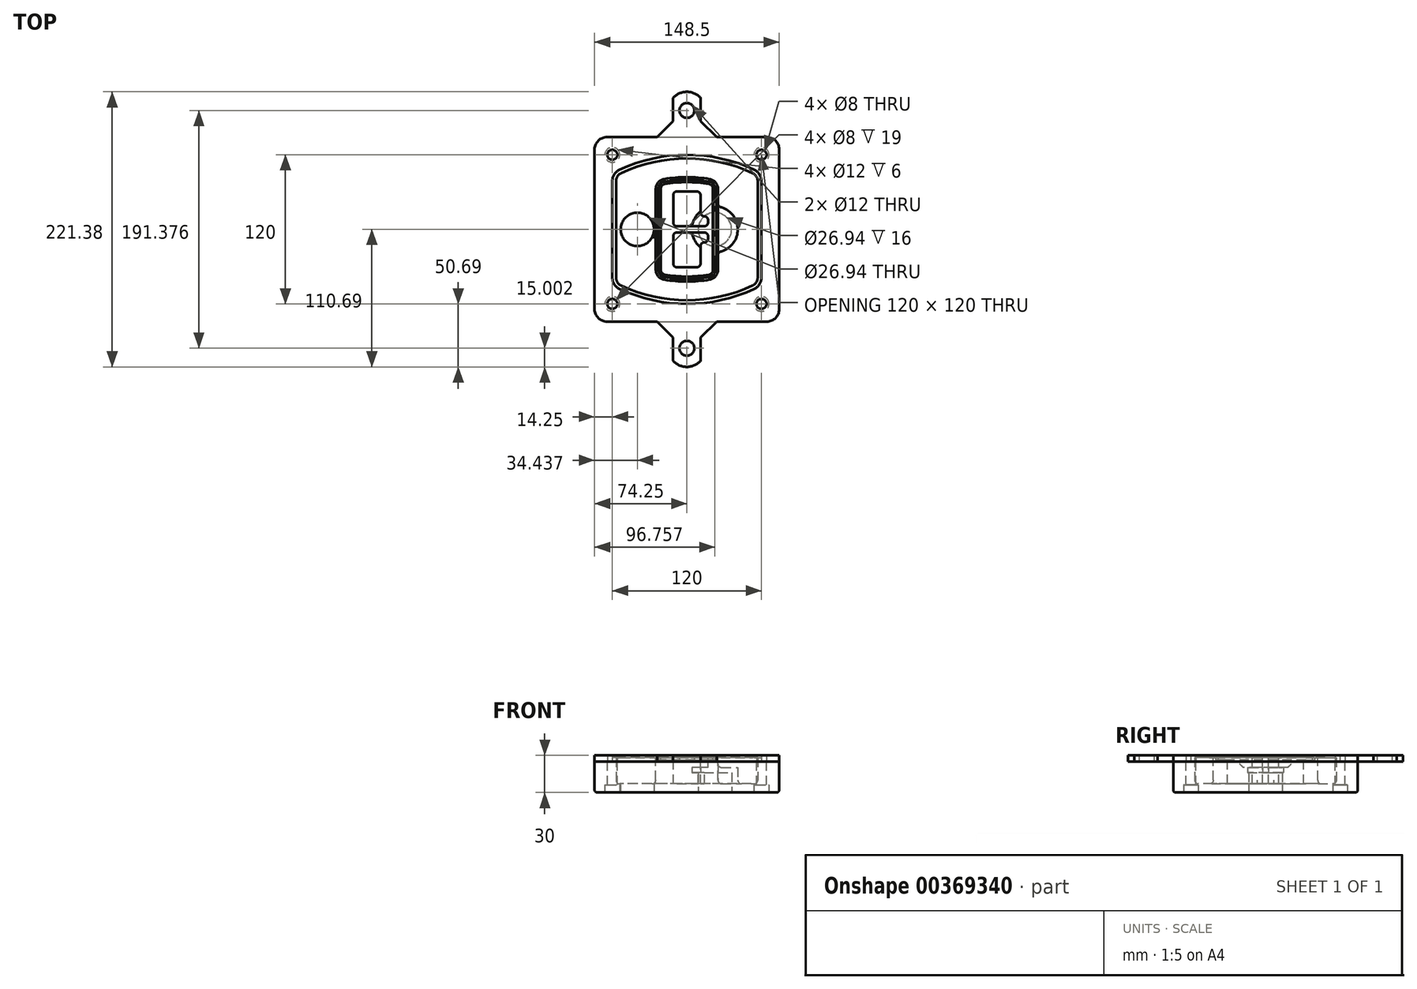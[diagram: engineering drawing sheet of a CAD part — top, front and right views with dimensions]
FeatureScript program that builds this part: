
annotation { "Feature Type Name" : "Feature", "Feature Type Description" : "" }
export const myFeature = defineFeature(function(context is Context, id is Id, definition is map)
    precondition{}
    {
        {
            var Q0;
            Q0=qCreatedBy(makeId("Top.planeOp"),FACE);
            var sketch = newSketch(context, id + "F0", { "sketchPlane" : qUnion([Q0])});
            skPoint(sketch, "E0.rect.middle", {"position": v(0, 0) * mm});
            skLineSegment(sketch, "E1.bottom", {"start": v(-64.25, -74.25) * mm, "end": v(64.25, -74.25) * mm});
            skLineSegment(sketch, "E1.top", {"start": v(-64.25, 74.25) * mm, "end": v(64.25, 74.25) * mm});
            skLineSegment(sketch, "E1.left", {"start": v(-74.25, -64.25) * mm, "end": v(-74.25, 64.25) * mm});
            skLineSegment(sketch, "E1.right", {"start": v(74.25, -64.25) * mm, "end": v(74.25, 64.25) * mm});
            skLineSegment(sketch, "E2", {"start": v(-74.25, 74.25) * mm, "end": v(74.25, -74.25) * mm, "construction": true});
            skLineSegment(sketch, "E3", {"start": v(74.25, 74.25) * mm, "end": v(-74.25, -74.25) * mm, "construction": true});
            skCircle(sketch, "E4", {"center": v(-60, 60) * mm, "radius": 4 * mm});
            skCircle(sketch, "E5", {"center": v(60, 60) * mm, "radius": 4 * mm});
            skCircle(sketch, "E6", {"center": v(60, -60) * mm, "radius": 4 * mm});
            skCircle(sketch, "E7", {"center": v(-60, -60) * mm, "radius": 4 * mm});
            skLineSegment(sketch, "E8", {"start": v(-60, 60) * mm, "end": v(60, 60) * mm, "construction": true});
            skLineSegment(sketch, "E9", {"start": v(60, 60) * mm, "end": v(60, -60) * mm, "construction": true});
            skLineSegment(sketch, "E10", {"start": v(60, -60) * mm, "end": v(-60, -60) * mm, "construction": true});
            skLineSegment(sketch, "E11", {"start": v(-60, -60) * mm, "end": v(-60, 60) * mm, "construction": true});
            skLineSegment(sketch, "E12", {"start": v(-60, 38.83) * mm, "end": v(-60, -38.83) * mm});
            skLineSegment(sketch, "E13", {"start": v(60, 38.83) * mm, "end": v(60, -38.83) * mm});
            skArc(sketch, "E14", {"start": v(54.26, 47.88) * mm, "mid": v(0, 60) * mm, "end": v(-54.26, 47.88) * mm});
            skArc(sketch, "E15", {"start": v(-54.26, -47.88) * mm, "mid": v(0, -60) * mm, "end": v(54.26, -47.88) * mm});
            skLineSegment(sketch, "E16", {"start": v(-60, 0) * mm, "end": v(60, 0) * mm, "construction": true});
            skPoint(sketch, "E17.visualSharp", {"position": v(-60, -45) * mm});
            skArc(sketch, "E17.filletArc", {"start": v(-60, -38.83) * mm, "mid": v(-58.44, -44.2) * mm, "end": v(-54.26, -47.88) * mm});
            skPoint(sketch, "E18.visualSharp", {"position": v(-60, 45) * mm});
            skArc(sketch, "E18.filletArc", {"start": v(-54.26, 47.88) * mm, "mid": v(-58.44, 44.2) * mm, "end": v(-60, 38.83) * mm});
            skPoint(sketch, "E19.visualSharp", {"position": v(60, 45) * mm});
            skArc(sketch, "E19.filletArc", {"start": v(60, 38.83) * mm, "mid": v(58.44, 44.2) * mm, "end": v(54.26, 47.88) * mm});
            skPoint(sketch, "E20.visualSharp", {"position": v(60, -45) * mm});
            skArc(sketch, "E20.filletArc", {"start": v(54.26, -47.88) * mm, "mid": v(58.44, -44.2) * mm, "end": v(60, -38.83) * mm});
            skPoint(sketch, "E21.visualSharp", {"position": v(-74.25, 74.25) * mm});
            skArc(sketch, "E21.filletArc", {"start": v(-64.25, 74.25) * mm, "mid": v(-71.32, 71.32) * mm, "end": v(-74.25, 64.25) * mm});
            skPoint(sketch, "E22.visualSharp", {"position": v(74.25, 74.25) * mm});
            skArc(sketch, "E22.filletArc", {"start": v(74.25, 64.25) * mm, "mid": v(71.32, 71.32) * mm, "end": v(64.25, 74.25) * mm});
            skPoint(sketch, "E23.visualSharp", {"position": v(74.25, -74.25) * mm});
            skArc(sketch, "E23.filletArc", {"start": v(64.25, -74.25) * mm, "mid": v(71.32, -71.32) * mm, "end": v(74.25, -64.25) * mm});
            skPoint(sketch, "E24.visualSharp", {"position": v(-74.25, -74.25) * mm});
            skArc(sketch, "E24.filletArc", {"start": v(-74.25, -64.25) * mm, "mid": v(-71.32, -71.32) * mm, "end": v(-64.25, -74.25) * mm});
            skArc(sketch, "E25.0", {"start": v(57, 38.83) * mm, "mid": v(55.9, 42.58) * mm, "end": v(52.98, 45.17) * mm});
            skLineSegment(sketch, "E25.1", {"start": v(57, 38.83) * mm, "end": v(57, -38.83) * mm});
            skArc(sketch, "E25.2", {"start": v(52.98, -45.17) * mm, "mid": v(55.9, -42.58) * mm, "end": v(57, -38.83) * mm});
            skArc(sketch, "E25.3", {"start": v(-52.98, -45.17) * mm, "mid": v(0, -57) * mm, "end": v(52.98, -45.17) * mm});
            skArc(sketch, "E25.4", {"start": v(-57, -38.83) * mm, "mid": v(-55.9, -42.58) * mm, "end": v(-52.98, -45.17) * mm});
            skArc(sketch, "E25.5", {"start": v(52.98, 45.17) * mm, "mid": v(0, 57) * mm, "end": v(-52.98, 45.17) * mm});
            skLineSegment(sketch, "E25.6", {"start": v(-57, 38.83) * mm, "end": v(-57, -38.83) * mm});
            skArc(sketch, "E25.7", {"start": v(-52.98, 45.17) * mm, "mid": v(-55.9, 42.58) * mm, "end": v(-57, 38.83) * mm});
            skArc(sketch, "E26.0", {"start": v(-55.96, 51.5) * mm, "mid": v(-61.82, 46.33) * mm, "end": v(-64, 38.83) * mm});
            skArc(sketch, "E26.1", {"start": v(55.96, 51.5) * mm, "mid": v(0, 64) * mm, "end": v(-55.96, 51.5) * mm});
            skArc(sketch, "E26.2", {"start": v(64, 38.83) * mm, "mid": v(61.82, 46.33) * mm, "end": v(55.96, 51.5) * mm});
            skLineSegment(sketch, "E26.3", {"start": v(64, 38.83) * mm, "end": v(64, -38.83) * mm});
            skArc(sketch, "E26.4", {"start": v(55.96, -51.5) * mm, "mid": v(61.82, -46.33) * mm, "end": v(64, -38.83) * mm});
            skLineSegment(sketch, "E26.5", {"start": v(-64, 38.83) * mm, "end": v(-64, -38.83) * mm});
            skArc(sketch, "E26.6", {"start": v(-55.96, -51.5) * mm, "mid": v(0, -64) * mm, "end": v(55.96, -51.5) * mm});
            skArc(sketch, "E26.7", {"start": v(-64, -38.83) * mm, "mid": v(-61.82, -46.33) * mm, "end": v(-55.96, -51.5) * mm});
            skSolve(sketch);
        }
        {
            var Q0;
            Q0=makeQuery(id+"F0.imprint","IMPRINT",FACE,{"disambiguationData":[TD([[makeQuery(id+"F0.imprint","IMPRINT",EDGE,{"derivedFrom":sQuery(id+"F0.wireOp",EDGE,"E1.bottom")}),1.0]])]});
            var Q1;
            Q1=makeQuery(id+"F0.imprint","IMPRINT",FACE,{"disambiguationData":[TD([[makeQuery(id+"F0.imprint","IMPRINT",EDGE,{"derivedFrom":sQuery(id+"F0.wireOp",EDGE,"E12")}),1.0]])]});
            var Q2;
            Q2=makeQuery(id+"F0.imprint","IMPRINT",FACE,{"disambiguationData":[TD([[makeQuery(id+"F0.imprint","IMPRINT",EDGE,{"derivedFrom":sQuery(id+"F0.wireOp",EDGE,"E25.0")}),1.0]])]});
            var Q3;
            Q3=makeQuery(id+"F0.imprint","IMPRINT",FACE,{"disambiguationData":[TD([[makeQuery(id+"F0.imprint","IMPRINT",EDGE,{"derivedFrom":sQuery(id+"F0.wireOp",EDGE,"E12")}),-1.0]])]});
            extrude(context, id + "F1", {"entities" : qUnion([Q0, Q1, Q2, Q3]), "oppositeDirection" : true, "depth" : 25 * mm});
        }
        {
            var Q0;
            Q0=makeQuery(id+"F0.imprint","IMPRINT",FACE,{"disambiguationData":[TD([[makeQuery(id+"F0.imprint","IMPRINT",EDGE,{"derivedFrom":sQuery(id+"F0.wireOp",EDGE,"E12")}),1.0]])]});
            extrude(context, id + "F2", {"entities" : qUnion([Q0]), "operationType" : NewBodyOperationType.ADD, "depth" : 3 * mm});
        }
        {
            var Q0;
            Q0=makeQuery(id+"F0.imprint","IMPRINT",FACE,{"disambiguationData":[TD([[makeQuery(id+"F0.imprint","IMPRINT",EDGE,{"derivedFrom":sQuery(id+"F0.wireOp",EDGE,"E25.0")}),1.0]])]});
            extrude(context, id + "F3", {"entities" : qUnion([Q0]), "operationType" : NewBodyOperationType.REMOVE, "oppositeDirection" : true, "depth" : 18 * mm});
        }
        {
            var Q0;
            Q0=makeQuery(id+"F2.opExtrude","CAP_FACE",FACE,{"disambiguationData":[OSD([sQuery(id+"F0.wireOp",EDGE,"E12"),sQuery(id+"F0.wireOp",EDGE,"E13"),sQuery(id+"F0.wireOp",EDGE,"E14"),sQuery(id+"F0.wireOp",EDGE,"E15"),sQuery(id+"F0.wireOp",EDGE,"E17.filletArc"),sQuery(id+"F0.wireOp",EDGE,"E18.filletArc"),sQuery(id+"F0.wireOp",EDGE,"E19.filletArc"),sQuery(id+"F0.wireOp",EDGE,"E20.filletArc"),sQuery(id+"F0.wireOp",EDGE,"E25.0"),sQuery(id+"F0.wireOp",EDGE,"E25.1"),sQuery(id+"F0.wireOp",EDGE,"E25.2"),sQuery(id+"F0.wireOp",EDGE,"E25.3"),sQuery(id+"F0.wireOp",EDGE,"E25.4"),sQuery(id+"F0.wireOp",EDGE,"E25.5"),sQuery(id+"F0.wireOp",EDGE,"E25.6"),sQuery(id+"F0.wireOp",EDGE,"E25.7")])],"isStart":false});
            var sketch = newSketch(context, id + "F4", { "sketchPlane" : qUnion([Q0])});
            skArc(sketch, "E27.0", {"start": v(-18.34, -40.45) * mm, "mid": v(0, -42) * mm, "end": v(18.34, -40.45) * mm});
            skArc(sketch, "E28.0", {"start": v(18.34, 40.45) * mm, "mid": v(0, 42) * mm, "end": v(-18.34, 40.45) * mm});
            skLineSegment(sketch, "E29", {"start": v(-25, 32.57) * mm, "end": v(-25, -32.57) * mm});
            skLineSegment(sketch, "E30", {"start": v(25, 32.57) * mm, "end": v(25, -32.57) * mm});
            skLineSegment(sketch, "E31", {"start": v(-25, 39.1) * mm, "end": v(25, 39.1) * mm, "construction": true});
            skLineSegment(sketch, "E32", {"start": v(-25, -39.1) * mm, "end": v(25, -39.1) * mm, "construction": true});
            skPoint(sketch, "E33.visualSharp", {"position": v(-25, 39.1) * mm});
            skArc(sketch, "E33.filletArc", {"start": v(-18.34, 40.45) * mm, "mid": v(-23.11, 37.73) * mm, "end": v(-25, 32.57) * mm});
            skPoint(sketch, "E34.visualSharp", {"position": v(25, 39.1) * mm});
            skArc(sketch, "E34.filletArc", {"start": v(25, 32.57) * mm, "mid": v(23.11, 37.73) * mm, "end": v(18.34, 40.45) * mm});
            skPoint(sketch, "E35.visualSharp", {"position": v(25, -39.1) * mm});
            skArc(sketch, "E35.filletArc", {"start": v(18.34, -40.45) * mm, "mid": v(23.11, -37.73) * mm, "end": v(25, -32.57) * mm});
            skPoint(sketch, "E36.visualSharp", {"position": v(-25, -39.1) * mm});
            skArc(sketch, "E36.filletArc", {"start": v(-25, -32.57) * mm, "mid": v(-23.11, -37.73) * mm, "end": v(-18.34, -40.45) * mm});
            skArc(sketch, "E37.0", {"start": v(52.98, 45.17) * mm, "mid": v(0, 57) * mm, "end": v(-52.98, 45.17) * mm});
            skArc(sketch, "E37.1", {"start": v(-52.98, 45.17) * mm, "mid": v(-55.9, 42.58) * mm, "end": v(-57, 38.83) * mm});
            skLineSegment(sketch, "E37.2", {"start": v(-57, 38.83) * mm, "end": v(-57, -38.83) * mm});
            skArc(sketch, "E37.3", {"start": v(-57, -38.83) * mm, "mid": v(-55.9, -42.58) * mm, "end": v(-52.98, -45.17) * mm});
            skArc(sketch, "E37.4", {"start": v(-52.98, -45.17) * mm, "mid": v(0, -57) * mm, "end": v(52.98, -45.17) * mm});
            skArc(sketch, "E37.5", {"start": v(52.98, -45.17) * mm, "mid": v(55.9, -42.58) * mm, "end": v(57, -38.83) * mm});
            skLineSegment(sketch, "E37.6", {"start": v(57, 38.83) * mm, "end": v(57, -38.83) * mm});
            skArc(sketch, "E37.7", {"start": v(57, 38.83) * mm, "mid": v(55.9, 42.58) * mm, "end": v(52.98, 45.17) * mm});
            skLineSegment(sketch, "E38.0", {"start": v(23, 32.57) * mm, "end": v(23, -32.57) * mm});
            skArc(sketch, "E38.1", {"start": v(18, -38.48) * mm, "mid": v(21.58, -36.44) * mm, "end": v(23, -32.57) * mm});
            skArc(sketch, "E38.2", {"start": v(-18, -38.48) * mm, "mid": v(0, -40) * mm, "end": v(18, -38.48) * mm});
            skArc(sketch, "E38.3", {"start": v(-23, -32.57) * mm, "mid": v(-21.58, -36.44) * mm, "end": v(-18, -38.48) * mm});
            skLineSegment(sketch, "E38.4", {"start": v(-23, 32.57) * mm, "end": v(-23, -32.57) * mm});
            skArc(sketch, "E38.5", {"start": v(23, 32.57) * mm, "mid": v(21.58, 36.44) * mm, "end": v(18, 38.48) * mm});
            skArc(sketch, "E38.6", {"start": v(-18, 38.48) * mm, "mid": v(-21.58, 36.44) * mm, "end": v(-23, 32.57) * mm});
            skArc(sketch, "E38.7", {"start": v(18, 38.48) * mm, "mid": v(0, 40) * mm, "end": v(-18, 38.48) * mm});
            skArc(sketch, "E39.0", {"start": v(21, 32.57) * mm, "mid": v(20.06, 35.15) * mm, "end": v(17.67, 36.5) * mm});
            skLineSegment(sketch, "E39.1", {"start": v(21, 32.57) * mm, "end": v(21, -32.57) * mm});
            skArc(sketch, "E39.2", {"start": v(17.67, -36.5) * mm, "mid": v(20.06, -35.15) * mm, "end": v(21, -32.57) * mm});
            skArc(sketch, "E39.3", {"start": v(-17.67, -36.5) * mm, "mid": v(0, -38) * mm, "end": v(17.67, -36.5) * mm});
            skArc(sketch, "E39.4", {"start": v(-21, -32.57) * mm, "mid": v(-20.06, -35.15) * mm, "end": v(-17.67, -36.5) * mm});
            skArc(sketch, "E39.5", {"start": v(17.67, 36.5) * mm, "mid": v(0, 38) * mm, "end": v(-17.67, 36.5) * mm});
            skLineSegment(sketch, "E39.6", {"start": v(-21, 32.57) * mm, "end": v(-21, -32.57) * mm});
            skArc(sketch, "E39.7", {"start": v(-17.67, 36.5) * mm, "mid": v(-20.06, 35.15) * mm, "end": v(-21, 32.57) * mm});
            skLineSegment(sketch, "E40", {"start": v(-25, 0) * mm, "end": v(25, 0) * mm, "construction": true});
            skLineSegment(sketch, "E41", {"start": v(-11, 5.5) * mm, "end": v(-11, 27.5) * mm});
            skLineSegment(sketch, "E42", {"start": v(-8, 30.5) * mm, "end": v(8, 30.5) * mm});
            skLineSegment(sketch, "E43", {"start": v(11, 27.5) * mm, "end": v(11, 13.5) * mm});
            skLineSegment(sketch, "E44", {"start": v(14, 10.5) * mm, "end": v(14, 10.5) * mm});
            skLineSegment(sketch, "E45", {"start": v(17, 7.5) * mm, "end": v(17, 5.5) * mm});
            skLineSegment(sketch, "E46", {"start": v(14, 2.5) * mm, "end": v(-8, 2.5) * mm});
            skPoint(sketch, "E47.visualSharp", {"position": v(-11, 30.5) * mm});
            skArc(sketch, "E47.filletArc", {"start": v(-8, 30.5) * mm, "mid": v(-10.12, 29.62) * mm, "end": v(-11, 27.5) * mm});
            skPoint(sketch, "E48.visualSharp", {"position": v(11, 30.5) * mm});
            skArc(sketch, "E48.filletArc", {"start": v(11, 27.5) * mm, "mid": v(10.12, 29.62) * mm, "end": v(8, 30.5) * mm});
            skPoint(sketch, "E49.visualSharp", {"position": v(11, 10.5) * mm});
            skArc(sketch, "E49.filletArc", {"start": v(11, 13.5) * mm, "mid": v(11.88, 11.38) * mm, "end": v(14, 10.5) * mm});
            skPoint(sketch, "E50.visualSharp", {"position": v(17, 10.5) * mm});
            skArc(sketch, "E50.filletArc", {"start": v(17, 7.5) * mm, "mid": v(16.12, 9.62) * mm, "end": v(14, 10.5) * mm});
            skPoint(sketch, "E51.visualSharp", {"position": v(17, 2.5) * mm});
            skArc(sketch, "E51.filletArc", {"start": v(14, 2.5) * mm, "mid": v(16.12, 3.38) * mm, "end": v(17, 5.5) * mm});
            skPoint(sketch, "E52.visualSharp", {"position": v(-11, 2.5) * mm});
            skArc(sketch, "E52.filletArc", {"start": v(-11, 5.5) * mm, "mid": v(-10.12, 3.38) * mm, "end": v(-8, 2.5) * mm});
            skLineSegment(sketch, "E53.0.MirrorCS", {"start": v(14, -2.5) * mm, "end": v(-8, -2.5) * mm});
            skArc(sketch, "E54.0.MirrorCS", {"start": v(-11, -5.5) * mm, "mid": v(-10.12, -3.38) * mm, "end": v(-8, -2.5) * mm});
            skLineSegment(sketch, "E55.0.MirrorCS", {"start": v(-11, -5.5) * mm, "end": v(-11, -27.5) * mm});
            skArc(sketch, "E56.0.MirrorCS", {"start": v(-8, -30.5) * mm, "mid": v(-10.12, -29.62) * mm, "end": v(-11, -27.5) * mm});
            skLineSegment(sketch, "E57.0.MirrorCS", {"start": v(-8, -30.5) * mm, "end": v(8, -30.5) * mm});
            skArc(sketch, "E58.0.MirrorCS", {"start": v(11, -27.5) * mm, "mid": v(10.12, -29.62) * mm, "end": v(8, -30.5) * mm});
            skLineSegment(sketch, "E59.0.MirrorCS", {"start": v(11, -27.5) * mm, "end": v(11, -13.5) * mm});
            skArc(sketch, "E60.0.MirrorCS", {"start": v(11, -13.5) * mm, "mid": v(11.88, -11.38) * mm, "end": v(14, -10.5) * mm});
            skArc(sketch, "E61.0.MirrorCS", {"start": v(17, -7.5) * mm, "mid": v(16.12, -9.62) * mm, "end": v(14, -10.5) * mm});
            skLineSegment(sketch, "E62.0.MirrorCS", {"start": v(17, -7.5) * mm, "end": v(17, -5.5) * mm});
            skArc(sketch, "E63.0.MirrorCS", {"start": v(14, -2.5) * mm, "mid": v(16.12, -3.38) * mm, "end": v(17, -5.5) * mm});
            skSolve(sketch);
        }
        {
            var Q0;
            Q0=makeQuery(id+"F4.imprint","IMPRINT",FACE,{"disambiguationData":[TD([[makeQuery(id+"F4.imprint","IMPRINT",EDGE,{"derivedFrom":sQuery(id+"F4.wireOp",EDGE,"E27.0")}),1.0]])]});
            var Q1;
            Q1=makeQuery(id+"F4.imprint","IMPRINT",FACE,{"disambiguationData":[TD([[makeQuery(id+"F4.imprint","IMPRINT",EDGE,{"derivedFrom":sQuery(id+"F4.wireOp",EDGE,"E38.0")}),-1.0]])]});
            var Q2;
            Q2=makeQuery(id+"F4.imprint","IMPRINT",FACE,{"disambiguationData":[TD([[makeQuery(id+"F4.imprint","IMPRINT",EDGE,{"derivedFrom":sQuery(id+"F4.wireOp",EDGE,"E39.0")}),1.0]])]});
            extrude(context, id + "F5", {"entities" : qUnion([Q0, Q1, Q2]), "operationType" : NewBodyOperationType.ADD, "endBound" : BoundingType.UP_TO_NEXT, "oppositeDirection" : true, "depth" : 25 * mm});
        }
        {
            var Q0;
            Q0=makeQuery(id+"F4.imprint","IMPRINT",FACE,{"disambiguationData":[TD([[makeQuery(id+"F4.imprint","IMPRINT",EDGE,{"derivedFrom":sQuery(id+"F4.wireOp",EDGE,"E38.0")}),-1.0]])]});
            extrude(context, id + "F6", {"entities" : qUnion([Q0]), "operationType" : NewBodyOperationType.REMOVE, "oppositeDirection" : true, "depth" : 2 * mm});
        }
        {
            var Q0;
            Q0=makeQuery(id+"F1.opExtrude","CAP_FACE",FACE,{"disambiguationData":[OSD([sQuery(id+"F0.wireOp",EDGE,"E1.bottom"),sQuery(id+"F0.wireOp",EDGE,"E1.top"),sQuery(id+"F0.wireOp",EDGE,"E1.left"),sQuery(id+"F0.wireOp",EDGE,"E1.right"),sQuery(id+"F0.wireOp",EDGE,"E4"),sQuery(id+"F0.wireOp",EDGE,"E5"),sQuery(id+"F0.wireOp",EDGE,"E6"),sQuery(id+"F0.wireOp",EDGE,"E7"),sQuery(id+"F0.wireOp",EDGE,"E21.filletArc"),sQuery(id+"F0.wireOp",EDGE,"E22.filletArc"),sQuery(id+"F0.wireOp",EDGE,"E23.filletArc"),sQuery(id+"F0.wireOp",EDGE,"E24.filletArc")])],"isStart":false});
            var sketch = newSketch(context, id + "F7", { "sketchPlane" : qUnion([Q0])});
            skCircle(sketch, "E64", {"center": v(22.5, 0) * mm, "radius": 13.47 * mm});
            skCircle(sketch, "E65", {"center": v(-39.81, 0) * mm, "radius": 13.47 * mm});
            skLineSegment(sketch, "E66", {"start": v(74.25, 0) * mm, "end": v(-74.25, 0) * mm});
            skCircle(sketch, "E67", {"center": v(22.5, 0) * mm, "radius": 18.47 * mm});
            skCircle(sketch, "E68", {"center": v(60, -60) * mm, "radius": 6 * mm});
            skCircle(sketch, "E69", {"center": v(-60, -60) * mm, "radius": 6 * mm});
            skCircle(sketch, "E70", {"center": v(-60, 60) * mm, "radius": 6 * mm});
            skCircle(sketch, "E71", {"center": v(60, 60) * mm, "radius": 6 * mm});
            skSolve(sketch);
        }
        {
            var Q0;
            {var subQ1=sQuery(id+"F7.wireOp",EDGE,"E66");var subQ4=sQuery(id+"F7.wireOp",EDGE,"E64");var subQ6=makeQuery(id+"F7.imprint","INTERSECT",VERTEX,{"disambiguationData":[OD(0.0)],"derivedFrom":[subQ4,subQ1]});Q0=makeQuery(id+"F7.imprint","IMPRINT",FACE,{"disambiguationData":[TD([[makeQuery(id+"F7.imprint","IMPRINT",EDGE,{"disambiguationData":[TD([[subQ6,-1.0]])],"derivedFrom":subQ4}),-1.0]])]});}
            var Q1;
            {var subQ0=sQuery(id+"F7.wireOp",EDGE,"E66");var subQ1=sQuery(id+"F7.wireOp",EDGE,"E64");var subQ3=makeQuery(id+"F7.imprint","INTERSECT",VERTEX,{"disambiguationData":[OD(0.0)],"derivedFrom":[subQ1,subQ0]});Q1=makeQuery(id+"F7.imprint","IMPRINT",FACE,{"disambiguationData":[TD([[makeQuery(id+"F7.imprint","IMPRINT",EDGE,{"disambiguationData":[TD([[subQ3,-1.0]])],"derivedFrom":subQ1}),1.0]])]});}
            var Q2;
            {var subQ0=sQuery(id+"F7.wireOp",EDGE,"E66");var subQ1=sQuery(id+"F7.wireOp",EDGE,"E64");var subQ3=makeQuery(id+"F7.imprint","INTERSECT",VERTEX,{"disambiguationData":[OD(0.0)],"derivedFrom":[subQ1,subQ0]});Q2=makeQuery(id+"F7.imprint","IMPRINT",FACE,{"disambiguationData":[TD([[makeQuery(id+"F7.imprint","IMPRINT",EDGE,{"disambiguationData":[TD([[subQ3,1.0]])],"derivedFrom":subQ1}),1.0]])]});}
            var Q3;
            {var subQ1=sQuery(id+"F7.wireOp",EDGE,"E66");var subQ4=sQuery(id+"F7.wireOp",EDGE,"E64");var subQ6=makeQuery(id+"F7.imprint","INTERSECT",VERTEX,{"disambiguationData":[OD(0.0)],"derivedFrom":[subQ4,subQ1]});Q3=makeQuery(id+"F7.imprint","IMPRINT",FACE,{"disambiguationData":[TD([[makeQuery(id+"F7.imprint","IMPRINT",EDGE,{"disambiguationData":[TD([[subQ6,1.0]])],"derivedFrom":subQ4}),-1.0]])]});}
            extrude(context, id + "F8", {"entities" : qUnion([Q0, Q1, Q2, Q3]), "operationType" : NewBodyOperationType.ADD, "oppositeDirection" : true, "depth" : 20 * mm});
        }
        {
            var Q0;
            {var subQ0=sQuery(id+"F7.wireOp",EDGE,"E66");var subQ1=sQuery(id+"F7.wireOp",EDGE,"E64");var subQ3=makeQuery(id+"F7.imprint","INTERSECT",VERTEX,{"disambiguationData":[OD(0.0)],"derivedFrom":[subQ1,subQ0]});Q0=makeQuery(id+"F7.imprint","IMPRINT",FACE,{"disambiguationData":[TD([[makeQuery(id+"F7.imprint","IMPRINT",EDGE,{"disambiguationData":[TD([[subQ3,-1.0]])],"derivedFrom":subQ1}),1.0]])]});}
            var Q1;
            {var subQ0=sQuery(id+"F7.wireOp",EDGE,"E66");var subQ1=sQuery(id+"F7.wireOp",EDGE,"E64");var subQ3=makeQuery(id+"F7.imprint","INTERSECT",VERTEX,{"disambiguationData":[OD(0.0)],"derivedFrom":[subQ1,subQ0]});Q1=makeQuery(id+"F7.imprint","IMPRINT",FACE,{"disambiguationData":[TD([[makeQuery(id+"F7.imprint","IMPRINT",EDGE,{"disambiguationData":[TD([[subQ3,1.0]])],"derivedFrom":subQ1}),1.0]])]});}
            extrude(context, id + "F9", {"entities" : qUnion([Q0, Q1]), "operationType" : NewBodyOperationType.REMOVE, "oppositeDirection" : true, "depth" : 16 * mm});
        }
        {
            var Q0;
            {var subQ0=sQuery(id+"F7.wireOp",EDGE,"E66");var subQ1=sQuery(id+"F7.wireOp",EDGE,"E65");var subQ3=makeQuery(id+"F7.imprint","INTERSECT",VERTEX,{"disambiguationData":[OD(0.0)],"derivedFrom":[subQ1,subQ0]});Q0=makeQuery(id+"F7.imprint","IMPRINT",FACE,{"disambiguationData":[TD([[makeQuery(id+"F7.imprint","IMPRINT",EDGE,{"disambiguationData":[TD([[subQ3,-1.0]])],"derivedFrom":subQ1}),1.0]])]});}
            var Q1;
            {var subQ0=sQuery(id+"F7.wireOp",EDGE,"E66");var subQ1=sQuery(id+"F7.wireOp",EDGE,"E65");var subQ3=makeQuery(id+"F7.imprint","INTERSECT",VERTEX,{"disambiguationData":[OD(0.0)],"derivedFrom":[subQ1,subQ0]});Q1=makeQuery(id+"F7.imprint","IMPRINT",FACE,{"disambiguationData":[TD([[makeQuery(id+"F7.imprint","IMPRINT",EDGE,{"disambiguationData":[TD([[subQ3,1.0]])],"derivedFrom":subQ1}),1.0]])]});}
            extrude(context, id + "F10", {"entities" : qUnion([Q0, Q1]), "operationType" : NewBodyOperationType.REMOVE, "oppositeDirection" : true, "depth" : 25 * mm});
        }
        {
            var Q0;
            Q0=makeQuery(id+"F7.imprint","IMPRINT",FACE,{"disambiguationData":[TD([[makeQuery(id+"F7.imprint","IMPRINT",EDGE,{"derivedFrom":sQuery(id+"F7.wireOp",EDGE,"E68")}),1.0]])]});
            var Q1;
            Q1=makeQuery(id+"F7.imprint","IMPRINT",FACE,{"disambiguationData":[TD([[makeQuery(id+"F7.imprint","IMPRINT",EDGE,{"derivedFrom":makeQuery(id+"F1.opExtrude","CAP_EDGE",EDGE,{"disambiguationData":[OSD([sQuery(id+"F0.wireOp",EDGE,"E5")])],"isStart":false})}),-1.0]])]});
            var Q2;
            Q2=makeQuery(id+"F7.imprint","IMPRINT",FACE,{"disambiguationData":[TD([[makeQuery(id+"F7.imprint","IMPRINT",EDGE,{"derivedFrom":sQuery(id+"F7.wireOp",EDGE,"E69")}),1.0]])]});
            var Q3;
            Q3=makeQuery(id+"F7.imprint","IMPRINT",FACE,{"disambiguationData":[TD([[makeQuery(id+"F7.imprint","IMPRINT",EDGE,{"derivedFrom":makeQuery(id+"F1.opExtrude","CAP_EDGE",EDGE,{"disambiguationData":[OSD([sQuery(id+"F0.wireOp",EDGE,"E4")])],"isStart":false})}),-1.0]])]});
            var Q4;
            Q4=makeQuery(id+"F7.imprint","IMPRINT",FACE,{"disambiguationData":[TD([[makeQuery(id+"F7.imprint","IMPRINT",EDGE,{"derivedFrom":sQuery(id+"F7.wireOp",EDGE,"E70")}),1.0]])]});
            var Q5;
            Q5=makeQuery(id+"F7.imprint","IMPRINT",FACE,{"disambiguationData":[TD([[makeQuery(id+"F7.imprint","IMPRINT",EDGE,{"derivedFrom":makeQuery(id+"F1.opExtrude","CAP_EDGE",EDGE,{"disambiguationData":[OSD([sQuery(id+"F0.wireOp",EDGE,"E7")])],"isStart":false})}),-1.0]])]});
            var Q6;
            Q6=makeQuery(id+"F7.imprint","IMPRINT",FACE,{"disambiguationData":[TD([[makeQuery(id+"F7.imprint","IMPRINT",EDGE,{"derivedFrom":sQuery(id+"F7.wireOp",EDGE,"E71")}),1.0]])]});
            var Q7;
            Q7=makeQuery(id+"F7.imprint","IMPRINT",FACE,{"disambiguationData":[TD([[makeQuery(id+"F7.imprint","IMPRINT",EDGE,{"derivedFrom":makeQuery(id+"F1.opExtrude","CAP_EDGE",EDGE,{"disambiguationData":[OSD([sQuery(id+"F0.wireOp",EDGE,"E6")])],"isStart":false})}),-1.0]])]});
            extrude(context, id + "F11", {"entities" : qUnion([Q0, Q1, Q2, Q3, Q4, Q5, Q6, Q7]), "operationType" : NewBodyOperationType.REMOVE, "oppositeDirection" : true, "depth" : 6 * mm});
        }
        {
            var Q0;
            Q0=makeQuery(id+"F9.boolean.opBoolean","COPY",FACE,{"derivedFrom":makeQuery(id+"F9.opExtrude","CAP_FACE",FACE,{"disambiguationData":[OSD([sQuery(id+"F7.wireOp",EDGE,"E64")])],"isStart":false})});
            var sketch = newSketch(context, id + "F12", { "sketchPlane" : qUnion([Q0])});
            skArc(sketch, "E72.0", {"start": v(11, 14.45) * mm, "mid": v(6.45, 9.13) * mm, "end": v(4.2, 2.5) * mm});
            skArc(sketch, "E72.1", {"start": v(4.2, -2.5) * mm, "mid": v(6.45, -9.13) * mm, "end": v(11, -14.45) * mm});
            skLineSegment(sketch, "E73", {"start": v(4.2, -2.5) * mm, "end": v(14, -2.5) * mm});
            skLineSegment(sketch, "E74.0", {"start": v(14, 2.5) * mm, "end": v(4.2, 2.5) * mm});
            skArc(sketch, "E74.1", {"start": v(14, 2.5) * mm, "mid": v(16.12, 3.38) * mm, "end": v(17, 5.5) * mm});
            skLineSegment(sketch, "E74.2", {"start": v(17, 7.5) * mm, "end": v(17, 5.5) * mm});
            skArc(sketch, "E74.3", {"start": v(17, 7.5) * mm, "mid": v(16.12, 9.62) * mm, "end": v(14, 10.5) * mm});
            skArc(sketch, "E74.4", {"start": v(11, 13.5) * mm, "mid": v(11.88, 11.38) * mm, "end": v(14, 10.5) * mm});
            skLineSegment(sketch, "E74.5", {"start": v(11, 14.45) * mm, "end": v(11, 13.5) * mm});
            skLineSegment(sketch, "E74.7", {"start": v(14, -2.5) * mm, "end": v(4.2, -2.5) * mm});
            skArc(sketch, "E74.8", {"start": v(14, -2.5) * mm, "mid": v(16.12, -3.38) * mm, "end": v(17, -5.5) * mm});
            skLineSegment(sketch, "E74.9", {"start": v(17, -7.5) * mm, "end": v(17, -5.5) * mm});
            skArc(sketch, "E74.10", {"start": v(17, -7.5) * mm, "mid": v(16.12, -9.62) * mm, "end": v(14, -10.5) * mm});
            skArc(sketch, "E74.11", {"start": v(11, -13.5) * mm, "mid": v(11.88, -11.38) * mm, "end": v(14, -10.5) * mm});
            skLineSegment(sketch, "E74.12", {"start": v(11, -14.45) * mm, "end": v(11, -13.5) * mm});
            skPoint(sketch, "E75.orphan", {"position": v(11, -27.5) * mm});
            skPoint(sketch, "E76.orphan", {"position": v(-8, -2.5) * mm});
            skPoint(sketch, "E77.orphan", {"position": v(-8, 2.5) * mm});
            skPoint(sketch, "E78.orphan", {"position": v(11, 27.5) * mm});
            skSolve(sketch);
        }
        {
            var Q0;
            {var subQ7=sQuery(id+"F12.wireOp",EDGE,"E72.0");var subQ14=sQuery(id+"F12.wireOp",EDGE,"E72.1");var subQ16=sQuery(id+"F12.wireOp",EDGE,"E74.1");var subQ18=sQuery(id+"F12.wireOp",EDGE,"E74.8");Q0=qUnion([makeQuery(id+"F12.imprint","IMPRINT",FACE,{"disambiguationData":[TD([[makeQuery(id+"F12.imprint","IMPRINT",EDGE,{"derivedFrom":subQ7}),1.0]])]}),makeQuery(id+"F12.imprint","IMPRINT",FACE,{"disambiguationData":[TD([[makeQuery(id+"F12.imprint","IMPRINT",EDGE,{"derivedFrom":subQ14}),1.0]])]}),makeQuery(id+"F12.imprint","IMPRINT",FACE,{"disambiguationData":[TD([[makeQuery(id+"F12.imprint","IMPRINT",EDGE,{"derivedFrom":subQ16}),1.0]])]}),makeQuery(id+"F12.imprint","IMPRINT",FACE,{"disambiguationData":[TD([[makeQuery(id+"F12.imprint","IMPRINT",EDGE,{"derivedFrom":subQ18}),-1.0]])]})]);}
            var Q1;
            Q1=makeQuery(id+"F5.boolean.opBoolean","SPLIT",FACE,{"disambiguationData":[TD([makeQuery(id+"F5.opExtrude","SWEPT_FACE",FACE,{"disambiguationData":[OSD([sQuery(id+"F4.wireOp",EDGE,"E41")])]})])],"derivedFrom":makeQuery(id+"F3.boolean.opBoolean","COPY",FACE,{"derivedFrom":makeQuery(id+"F3.opExtrude","CAP_FACE",FACE,{"disambiguationData":[OSD([sQuery(id+"F0.wireOp",EDGE,"E25.0"),sQuery(id+"F0.wireOp",EDGE,"E25.1"),sQuery(id+"F0.wireOp",EDGE,"E25.2"),sQuery(id+"F0.wireOp",EDGE,"E25.3"),sQuery(id+"F0.wireOp",EDGE,"E25.4"),sQuery(id+"F0.wireOp",EDGE,"E25.5"),sQuery(id+"F0.wireOp",EDGE,"E25.6"),sQuery(id+"F0.wireOp",EDGE,"E25.7")])],"isStart":false})})});
            extrude(context, id + "F13", {"entities" : qUnion([Q0]), "operationType" : NewBodyOperationType.REMOVE, "endBound" : BoundingType.UP_TO_SURFACE, "endBoundEntityFace" : qUnion([Q1]), "depth" : 25 * mm});
        }
        {
            var Q0;
            Q0=makeQuery(id+"F3.boolean.opBoolean","COPY",EDGE,{"derivedFrom":makeQuery(id+"F3.opExtrude","CAP_EDGE",EDGE,{"disambiguationData":[OSD([sQuery(id+"F0.wireOp",EDGE,"E25.6")])],"isStart":false})});
            var Q1;
            Q1=makeQuery(id+"F8.boolean.opBoolean","INTERSECT",EDGE,{"derivedFrom":[makeQuery(id+"F5.opExtrude","SWEPT_FACE",FACE,{"disambiguationData":[OSD([sQuery(id+"F4.wireOp",EDGE,"E30")])]}),makeQuery(id+"F8.opExtrude","CAP_FACE",FACE,{"disambiguationData":[OSD([sQuery(id+"F7.wireOp",EDGE,"E67")])],"isStart":false})]});
            var Q2;
            Q2=makeQuery(id+"F8.boolean.opBoolean","INTERSECT",EDGE,{"disambiguationData":[OD(1.0)],"derivedFrom":[makeQuery(id+"F5.opExtrude","SWEPT_FACE",FACE,{"disambiguationData":[OSD([sQuery(id+"F4.wireOp",EDGE,"E30")])]}),makeQuery(id+"F8.opExtrude","SWEPT_FACE",FACE,{"disambiguationData":[OSD([sQuery(id+"F7.wireOp",EDGE,"E67")])]})]});
            var Q3;
            {var subQ0=sQuery(id+"F4.wireOp",EDGE,"E30");Q3=makeQuery(id+"F8.boolean.opBoolean","SPLIT",EDGE,{"disambiguationData":[TD([makeQuery(id+"F5.opExtrude","SWEPT_FACE",FACE,{"disambiguationData":[OSD([sQuery(id+"F4.wireOp",EDGE,"E35.filletArc")])]})])],"derivedFrom":makeQuery(id+"F5.opExtrude","CAP_EDGE",EDGE,{"disambiguationData":[OSD([subQ0])],"isStart":false})});}
            var Q4;
            {var subQ0=sQuery(id+"F0.wireOp",EDGE,"E25.7");var subQ1=sQuery(id+"F0.wireOp",EDGE,"E25.1");var subQ2=sQuery(id+"F0.wireOp",EDGE,"E25.6");var subQ3=sQuery(id+"F0.wireOp",EDGE,"E25.5");var subQ4=sQuery(id+"F0.wireOp",EDGE,"E25.4");var subQ5=sQuery(id+"F0.wireOp",EDGE,"E25.0");var subQ6=sQuery(id+"F0.wireOp",EDGE,"E25.2");var subQ7=sQuery(id+"F0.wireOp",EDGE,"E25.3");Q4=makeQuery(id+"F8.boolean.opBoolean","INTERSECT",EDGE,{"derivedFrom":[makeQuery(id+"F5.boolean.opBoolean","SPLIT",FACE,{"disambiguationData":[TD([makeQuery(id+"F2.opExtrude","SWEPT_FACE",FACE,{"disambiguationData":[OSD([subQ5])]})])],"derivedFrom":makeQuery(id+"F3.boolean.opBoolean","COPY",FACE,{"derivedFrom":makeQuery(id+"F3.opExtrude","CAP_FACE",FACE,{"disambiguationData":[OSD([subQ5,subQ1,subQ6,subQ7,subQ4,subQ3,subQ2,subQ0])],"isStart":false})})}),makeQuery(id+"F8.opExtrude","SWEPT_FACE",FACE,{"disambiguationData":[OSD([sQuery(id+"F7.wireOp",EDGE,"E67")])]})]});}
            var Q5;
            Q5=makeQuery(id+"F8.boolean.opBoolean","INTERSECT",EDGE,{"disambiguationData":[OD(0.0)],"derivedFrom":[makeQuery(id+"F5.opExtrude","SWEPT_FACE",FACE,{"disambiguationData":[OSD([sQuery(id+"F4.wireOp",EDGE,"E30")])]}),makeQuery(id+"F8.opExtrude","SWEPT_FACE",FACE,{"disambiguationData":[OSD([sQuery(id+"F7.wireOp",EDGE,"E67")])]})]});
            fillet(context, id + "F14", {"entities" : qUnion([Q0, Q1, Q2, Q3, Q4, Q5]), "radius" : 3 * mm, "tangentPropagation" : true, "allowEdgeOverflow" : false});
        }
        {
            var Q0;
            Q0=makeQuery(id+"F1.opExtrude","CAP_EDGE",EDGE,{"disambiguationData":[OSD([sQuery(id+"F0.wireOp",EDGE,"E1.bottom")])],"isStart":false});
            fillet(context, id + "F15", {"entities" : qUnion([Q0]), "radius" : 2 * mm, "tangentPropagation" : true, "allowEdgeOverflow" : false});
        }
        {
            var Q0;
            {var subQ0=sQuery(id+"F0.wireOp",EDGE,"E21.filletArc");var subQ1=sQuery(id+"F0.wireOp",EDGE,"E7");var subQ2=sQuery(id+"F0.wireOp",EDGE,"E6");var subQ3=sQuery(id+"F0.wireOp",EDGE,"E5");var subQ4=sQuery(id+"F0.wireOp",EDGE,"E4");var subQ5=sQuery(id+"F0.wireOp",EDGE,"E22.filletArc");var subQ6=sQuery(id+"F0.wireOp",EDGE,"E1.bottom");var subQ7=sQuery(id+"F0.wireOp",EDGE,"E1.right");var subQ8=sQuery(id+"F0.wireOp",EDGE,"E1.top");var subQ9=sQuery(id+"F0.wireOp",EDGE,"E1.left");var subQ10=sQuery(id+"F0.wireOp",EDGE,"E23.filletArc");var subQ11=sQuery(id+"F0.wireOp",EDGE,"E24.filletArc");Q0=makeQuery(id+"F2.boolean.opBoolean","SPLIT",FACE,{"disambiguationData":[TD([makeQuery(id+"F1.opExtrude","SWEPT_FACE",FACE,{"disambiguationData":[OSD([subQ6])]})])],"derivedFrom":makeQuery(id+"F1.opExtrude","CAP_FACE",FACE,{"disambiguationData":[OSD([subQ6,subQ8,subQ9,subQ7,subQ4,subQ3,subQ2,subQ1,subQ0,subQ5,subQ10,subQ11])],"isStart":true})});}
            var sketch = newSketch(context, id + "F16", { "sketchPlane" : qUnion([Q0])});
            skLineSegment(sketch, "E79", {"start": v(-23.77, 74.25) * mm, "end": v(-11.05, 86.98) * mm});
            skLineSegment(sketch, "E80", {"start": v(-11.05, 86.98) * mm, "end": v(-11.05, 105.84) * mm});
            skLineSegment(sketch, "E81", {"start": v(23.9, 74.25) * mm, "end": v(11.18, 86.98) * mm});
            skLineSegment(sketch, "E82", {"start": v(11.18, 86.98) * mm, "end": v(11.18, 105.69) * mm});
            skCircle(sketch, "E83", {"center": v(0, 95.69) * mm, "radius": 6 * mm});
            skArc(sketch, "E84", {"start": v(11.18, 105.69) * mm, "mid": v(0.1, 110.69) * mm, "end": v(-11.05, 105.84) * mm});
            skLineSegment(sketch, "E85", {"start": v(-87.79, 0) * mm, "end": v(91.83, 0) * mm});
            skPoint(sketch, "E85.startSnap0", {"position": v(-60, 0) * mm});
            skPoint(sketch, "E85.endSnap0", {"position": v(-74.25, 0) * mm});
            skLineSegment(sketch, "E86.MirrorCS", {"start": v(-23.77, -74.25) * mm, "end": v(-11.05, -86.98) * mm});
            skLineSegment(sketch, "E87.MirrorCS", {"start": v(-11.05, -86.98) * mm, "end": v(-11.05, -105.84) * mm});
            skArc(sketch, "E88.MirrorCS", {"start": v(11.18, -105.69) * mm, "mid": v(0.1, -110.69) * mm, "end": v(-11.05, -105.84) * mm});
            skLineSegment(sketch, "E89.MirrorCS", {"start": v(11.18, -86.98) * mm, "end": v(11.18, -105.69) * mm});
            skLineSegment(sketch, "E90.MirrorCS", {"start": v(23.9, -74.25) * mm, "end": v(11.18, -86.98) * mm});
            skCircle(sketch, "E91.MirrorC", {"center": v(0, -95.69) * mm, "radius": 6 * mm});
            skSolve(sketch);
        }
        {
            var Q0;
            {var subQ1=sQuery(id+"F16.wireOp",EDGE,"E79");Q0=makeQuery(id+"F16.imprint","IMPRINT",FACE,{"disambiguationData":[TD([[makeQuery(id+"F16.imprint","IMPRINT",EDGE,{"derivedFrom":subQ1}),-1.0]])]});}
            var Q1;
            Q1=makeQuery(id+"F16.imprint","IMPRINT",FACE,{"disambiguationData":[TD([[makeQuery(id+"F16.imprint","IMPRINT",EDGE,{"derivedFrom":makeQuery(id+"F1.opExtrude","CAP_EDGE",EDGE,{"disambiguationData":[OSD([sQuery(id+"F0.wireOp",EDGE,"E4")])],"isStart":true})}),-1.0]])]});
            var Q2;
            Q2=makeQuery(id+"F16.imprint","IMPRINT",FACE,{"disambiguationData":[TD([[makeQuery(id+"F16.imprint","IMPRINT",EDGE,{"derivedFrom":makeQuery(id+"F1.opExtrude","CAP_EDGE",EDGE,{"disambiguationData":[OSD([sQuery(id+"F0.wireOp",EDGE,"E6")])],"isStart":true})}),-1.0]])]});
            var Q3;
            {var subQ0=sQuery(id+"F16.wireOp",EDGE,"E86.MirrorCS");Q3=makeQuery(id+"F16.imprint","IMPRINT",FACE,{"disambiguationData":[TD([[makeQuery(id+"F16.imprint","IMPRINT",EDGE,{"derivedFrom":subQ0}),1.0]])]});}
            extrude(context, id + "F17", {"entities" : qUnion([Q0, Q1, Q2, Q3]), "depth" : 5 * mm});
        }
    });
